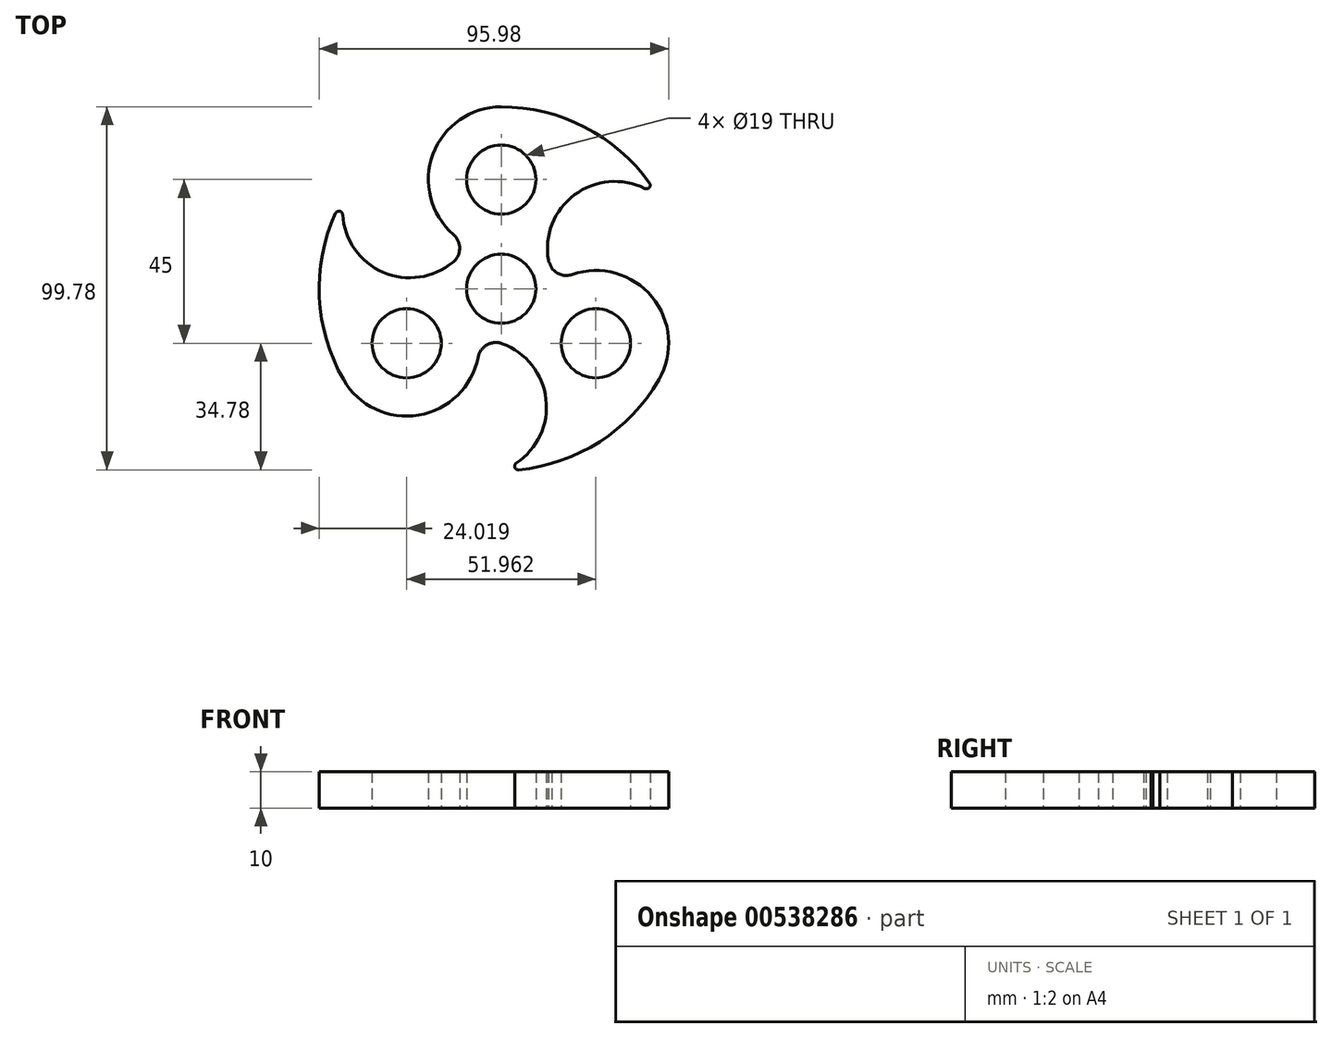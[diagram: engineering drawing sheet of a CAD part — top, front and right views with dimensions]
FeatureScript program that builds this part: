
annotation { "Feature Type Name" : "Feature", "Feature Type Description" : "" }
export const myFeature = defineFeature(function(context is Context, id is Id, definition is map)
    precondition{}
    {
        {
            var Q0;
            Q0=qCreatedBy(makeId("Top.planeOp"),FACE);
            var sketch = newSketch(context, id + "F0", { "sketchPlane" : qUnion([Q0])});
            skArc(sketch, "E0", {"start": v(4.78, -49.77) * mm, "mid": v(27.04, -42.05) * mm, "end": v(43.3, -25) * mm});
            skCircle(sketch, "E1", {"center": v(0, 0) * mm, "radius": 9.5 * mm});
            skCircle(sketch, "E2", {"center": v(0, 30) * mm, "radius": 9.5 * mm});
            skCircle(sketch, "E3.1.0", {"center": v(-25.98, -15) * mm, "radius": 9.5 * mm});
            skCircle(sketch, "E3.2.0", {"center": v(25.98, -15) * mm, "radius": 9.5 * mm});
            skArc(sketch, "E4", {"start": v(-12.98, 7.52) * mm, "mid": v(-12.98, 7.51) * mm, "end": v(-13, 7.5) * mm});
            skArc(sketch, "E5", {"start": v(39.45, 27.55) * mm, "mid": v(20.14, 25.81) * mm, "end": v(12.94, 7.8) * mm});
            skArc(sketch, "E6.1.0", {"start": v(-43.59, 20.4) * mm, "mid": v(-32.42, 4.53) * mm, "end": v(-13.22, 7.3) * mm});
            skPoint(sketch, "E7.orphan", {"position": v(43.3, 25) * mm});
            skArc(sketch, "E8.trimOffspring", {"start": v(4.13, -47.94) * mm, "mid": v(12.28, -30.34) * mm, "end": v(0.29, -15.1) * mm});
            skArc(sketch, "E9", {"start": v(43.3, -25) * mm, "mid": v(41.42, -2.29) * mm, "end": v(19.49, 3.92) * mm});
            skArc(sketch, "E10.1.0", {"start": v(0, 50) * mm, "mid": v(-18.73, 37.01) * mm, "end": v(-13.14, 14.92) * mm});
            skArc(sketch, "E10.2.0", {"start": v(-43.3, -25) * mm, "mid": v(-22.69, -34.73) * mm, "end": v(-6.35, -18.84) * mm});
            skArc(sketch, "E11.filletArc", {"start": v(-13.22, 7.3) * mm, "mid": v(-11.42, 11.1) * mm, "end": v(-13.14, 14.92) * mm});
            skArc(sketch, "E12.filletArc", {"start": v(12.94, 7.8) * mm, "mid": v(15.31, 4.34) * mm, "end": v(19.49, 3.92) * mm});
            skArc(sketch, "E13.filletArc", {"start": v(0.29, -15.1) * mm, "mid": v(-3.9, -15.44) * mm, "end": v(-6.35, -18.84) * mm});
            skArc(sketch, "E14.trimOffspring", {"start": v(40.71, 29.03) * mm, "mid": v(22.9, 44.45) * mm, "end": v(0, 50) * mm});
            skArc(sketch, "E15.trimOffspring", {"start": v(-45.5, 20.74) * mm, "mid": v(-49.94, -2.4) * mm, "end": v(-43.3, -25) * mm});
            skArc(sketch, "E16.filletArc", {"start": v(39.45, 27.55) * mm, "mid": v(40.66, 27.8) * mm, "end": v(40.71, 29.03) * mm});
            skLineSegment(sketch, "E17.trimOffspring", {"start": v(-13, 7.5) * mm, "end": v(-13, 7.5) * mm});
            skArc(sketch, "E18.filletArc", {"start": v(-43.59, 20.4) * mm, "mid": v(-44.4, 21.31) * mm, "end": v(-45.5, 20.74) * mm});
            skLineSegment(sketch, "E19.trimOffspring", {"start": v(0, -15) * mm, "end": v(0, -15) * mm});
            skPoint(sketch, "E20.visualSharp", {"position": v(0, -50) * mm});
            skArc(sketch, "E20.filletArc", {"start": v(4.13, -47.94) * mm, "mid": v(3.74, -49.11) * mm, "end": v(4.78, -49.77) * mm});
            skArc(sketch, "E21.trimOffspring", {"start": v(-0.02, -15) * mm, "mid": v(-0.01, -15) * mm, "end": v(0, -15) * mm});
            skArc(sketch, "E22.trimOffspring", {"start": v(13.93, 5.56) * mm, "mid": v(13.5, 6.53) * mm, "end": v(13, 7.48) * mm});
            skSolve(sketch);
        }
        {
            var Q0;
            Q0 = qSketchRegion(id + "F0", true);
            extrude(context, id + "F1", {"entities" : qUnion([Q0]), "depth" : 10 * mm, "offsetDistance" : 25 * mm});
        }
    });
